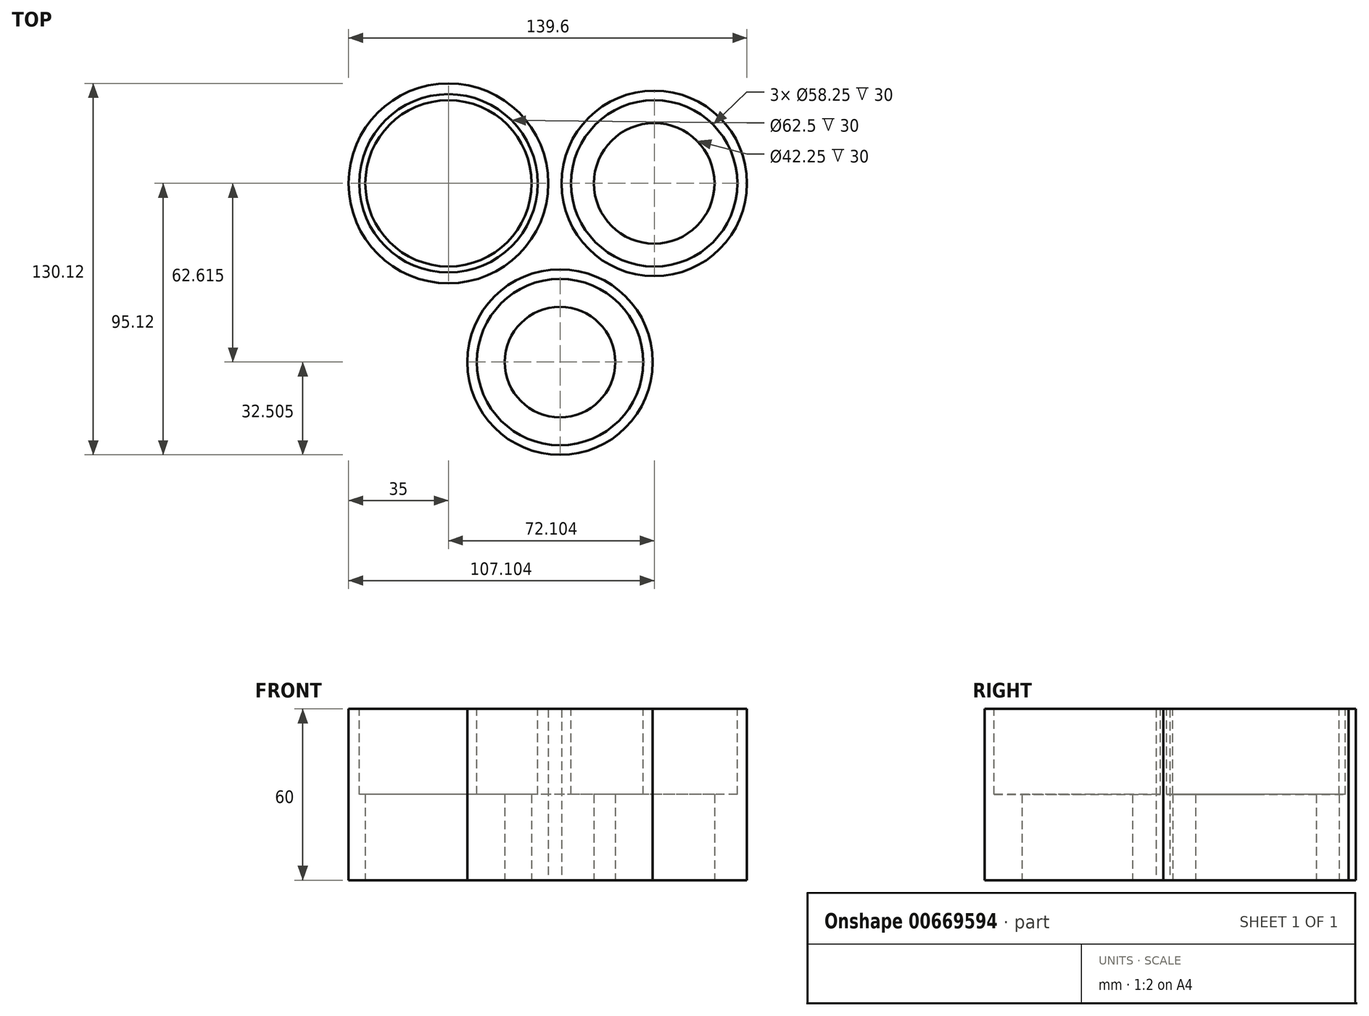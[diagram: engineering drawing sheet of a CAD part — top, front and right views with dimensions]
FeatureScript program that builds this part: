
annotation { "Feature Type Name" : "Feature", "Feature Type Description" : "" }
export const myFeature = defineFeature(function(context is Context, id is Id, definition is map)
    precondition{}
    {
        {
            var Q0;
            Q0=qCreatedBy(makeId("Top.planeOp"),FACE);
            var sketch = newSketch(context, id + "F0", { "sketchPlane" : qUnion([Q0])});
            skCircle(sketch, "E0", {"center": v(0, 0) * mm, "radius": 35 * mm});
            skCircle(sketch, "E1", {"center": v(72.1, 0) * mm, "radius": 32.5 * mm});
            skCircle(sketch, "E2", {"center": v(39.1, -62.62) * mm, "radius": 32.5 * mm});
            skSolve(sketch);
        }
        {
            var Q0;
            Q0 = qSketchRegion(id + "F0", true);
            extrude(context, id + "F1", {"entities" : qUnion([Q0]), "depth" : 60 * mm, "offsetDistance" : 25 * mm});
        }
        {
            var Q0;
            Q0=qCreatedBy(makeId("Top.planeOp"),FACE);
            var sketch = newSketch(context, id + "F2", { "sketchPlane" : qUnion([Q0])});
            skCircle(sketch, "E3", {"center": v(0, 0) * mm, "radius": 29.12 * mm});
            skCircle(sketch, "E4.0", {"center": v(72.1, 0) * mm, "radius": 32.5 * mm, "construction": true});
            skCircle(sketch, "E5", {"center": v(72.1, 0) * mm, "radius": 21.12 * mm});
            skCircle(sketch, "E6.0", {"center": v(39.1, -62.62) * mm, "radius": 32.5 * mm, "construction": true});
            skCircle(sketch, "E7", {"center": v(39.1, -62.62) * mm, "radius": 19.38 * mm});
            skSolve(sketch);
        }
        {
            var Q0;
            Q0 = qSketchRegion(id + "F2", true);
            var Q1;
            Q1=makeQuery(id+"F1.opExtrude","CAP_FACE",FACE,{"disambiguationData":[OSD([sQuery(id+"F0.wireOp",EDGE,"E0")])],"isStart":false});
            extrude(context, id + "F3", {"entities" : qUnion([Q0]), "operationType" : NewBodyOperationType.REMOVE, "endBound" : BoundingType.UP_TO_SURFACE, "depth" : 25 * mm, "endBoundEntityFace" : qUnion([Q1]), "offsetDistance" : 25 * mm});
        }
        {
            var Q0;
            Q0=makeQuery(id+"F1.opExtrude","CAP_FACE",FACE,{"disambiguationData":[OSD([sQuery(id+"F0.wireOp",EDGE,"E0")])],"isStart":false});
            cPlane(context, id + "F4", {"entities" : qUnion([Q0]), "cplaneType" : CPlaneType.OFFSET, "offset" : 0 * mm, "width" : 150 * mm, "height" : 150 * mm});
        }
        {
            var Q0;
            Q0=qCreatedBy(id+"F4.planeOp",FACE);
            var sketch = newSketch(context, id + "F5", { "sketchPlane" : qUnion([Q0])});
            skCircle(sketch, "E8", {"center": v(0, 0) * mm, "radius": 31.25 * mm});
            skCircle(sketch, "E9.0", {"center": v(72.1, 0) * mm, "radius": 21.12 * mm, "construction": true});
            skCircle(sketch, "E10", {"center": v(72.1, 0) * mm, "radius": 29.12 * mm});
            skCircle(sketch, "E11.0", {"center": v(39.1, -62.62) * mm, "radius": 32.5 * mm, "construction": true});
            skCircle(sketch, "E12", {"center": v(39.1, -62.62) * mm, "radius": 29.12 * mm});
            skSolve(sketch);
        }
        {
            var Q0;
            Q0 = qSketchRegion(id + "F5", true);
            extrude(context, id + "F6", {"entities" : qUnion([Q0]), "operationType" : NewBodyOperationType.REMOVE, "oppositeDirection" : true, "depth" : 30 * mm, "offsetDistance" : 25 * mm});
        }
    });
